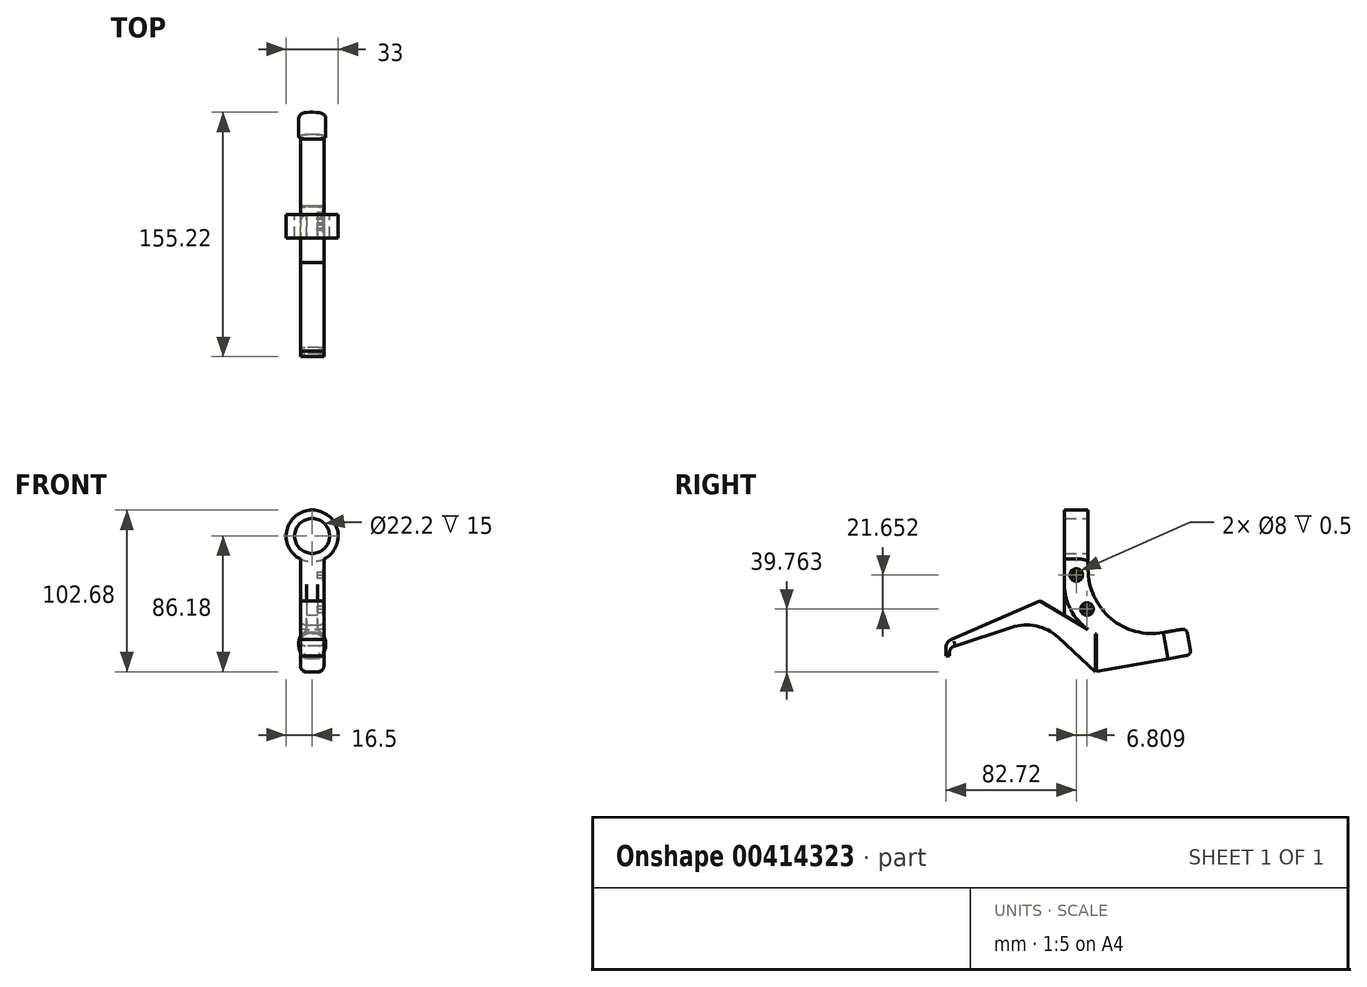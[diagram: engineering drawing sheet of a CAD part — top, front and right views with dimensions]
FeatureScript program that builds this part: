
annotation { "Feature Type Name" : "Feature", "Feature Type Description" : "" }
export const myFeature = defineFeature(function(context is Context, id is Id, definition is map)
    precondition{}
    {
        {
            var Q0;
            Q0=qCreatedBy(makeId("Front.planeOp"),FACE);
            var sketch = newSketch(context, id + "F0", { "sketchPlane" : qUnion([Q0])});
            skCircle(sketch, "E0", {"center": v(0, 0) * mm, "radius": 11.1 * mm});
            skCircle(sketch, "E1", {"center": v(0, 0) * mm, "radius": 16.5 * mm});
            skSolve(sketch);
        }
        {
            var Q0;
            Q0=makeQuery(id+"F0.imprint","IMPRINT",FACE,{"disambiguationData":[TD([[makeQuery(id+"F0.imprint","IMPRINT",EDGE,{"derivedFrom":sQuery(id+"F0.wireOp",EDGE,"E0")}),-1.0]])]});
            extrude(context, id + "F1", {"entities" : qUnion([Q0]), "endBound" : BoundingType.SYMMETRIC, "depth" : 15 * mm});
        }
        {
            var Q0;
            Q0=qCreatedBy(makeId("Right.planeOp"),FACE);
            var sketch = newSketch(context, id + "F2", { "sketchPlane" : qUnion([Q0])});
            skLineSegment(sketch, "E2", {"start": v(0, 0) * mm, "end": v(0, -54.97) * mm});
            skLineSegment(sketch, "E3", {"start": v(-7.5, 31.4) * mm, "end": v(-7.5, -50.53) * mm});
            skArc(sketch, "E4", {"start": v(-7.5, -30.7) * mm, "mid": v(-3.52, -46.9) * mm, "end": v(7.5, -59.41) * mm});
            skLineSegment(sketch, "E5", {"start": v(7.5, 51.74) * mm, "end": v(7.5, -21.27) * mm});
            skArc(sketch, "E6", {"start": v(7.5, -21.27) * mm, "mid": v(22.03, -52.44) * mm, "end": v(55.26, -61.34) * mm});
            skLineSegment(sketch, "E7", {"start": v(55.26, -61.34) * mm, "end": v(58.2, -78.08) * mm});
            skLineSegment(sketch, "E8", {"start": v(7.5, -59.41) * mm, "end": v(-23.15, -41.26) * mm});
            skLineSegment(sketch, "E9", {"start": v(-82.72, -70.49) * mm, "end": v(-82.72, -76.09) * mm});
            skLineSegment(sketch, "E10", {"start": v(-80.65, -76.09) * mm, "end": v(-80.65, -74.54) * mm});
            skLineSegment(sketch, "E11", {"start": v(-24.47, -52.49) * mm, "end": v(12.27, -86.18) * mm});
            skPoint(sketch, "E12.visualSharp", {"position": v(-80.65, -70.6) * mm});
            skArc(sketch, "E12.filletArc", {"start": v(-76.83, -69.68) * mm, "mid": v(-79.58, -71.45) * mm, "end": v(-80.65, -74.54) * mm});
            skPoint(sketch, "E13.visualSharp", {"position": v(-82.72, -66.82) * mm});
            skArc(sketch, "E13.filletArc", {"start": v(-79.22, -65.72) * mm, "mid": v(-81.75, -67.53) * mm, "end": v(-82.72, -70.49) * mm});
            skLineSegment(sketch, "E14.trimOffspring", {"start": v(12.77, -86.1) * mm, "end": v(58.2, -78.08) * mm});
            skLineSegment(sketch, "E15", {"start": v(-7.5, -13.2) * mm, "end": v(7.5, -13.2) * mm});
            skLineSegment(sketch, "E16", {"start": v(-82.72, -76.09) * mm, "end": v(-80.65, -76.09) * mm});
            skLineSegment(sketch, "E17", {"start": v(12.27, -86.18) * mm, "end": v(12.27, -62.22) * mm});
            skLineSegment(sketch, "E18", {"start": v(12.27, -62.22) * mm, "end": v(12.77, -62.22) * mm});
            skLineSegment(sketch, "E19", {"start": v(12.77, -62.22) * mm, "end": v(12.77, -86.1) * mm});
            skPoint(sketch, "E20.orphan", {"position": v(12.77, -86.18) * mm});
            skLineSegment(sketch, "E21", {"start": v(-79.22, -65.72) * mm, "end": v(-23.15, -41.26) * mm});
            skLineSegment(sketch, "E22", {"start": v(-76.83, -69.68) * mm, "end": v(-24.47, -52.49) * mm});
            skSolve(sketch);
        }
        {
            var Q0;
            {var subQ0=sQuery(id+"F2.wireOp",EDGE,"E15");var subQ1=sQuery(id+"F2.wireOp",EDGE,"E2");var subQ2=makeQuery(id+"F2.imprint","INTERSECT",VERTEX,{"derivedFrom":[subQ1,subQ0]});Q0=makeQuery(id+"F2.imprint","IMPRINT",FACE,{"disambiguationData":[TD([[makeQuery(id+"F2.imprint","IMPRINT",EDGE,{"disambiguationData":[TD([[subQ2,-1.0]])],"derivedFrom":subQ1}),-1.0]])]});}
            var Q1;
            {var subQ10=sQuery(id+"F2.wireOp",EDGE,"E6");Q1=makeQuery(id+"F2.imprint","IMPRINT",FACE,{"disambiguationData":[TD([[makeQuery(id+"F2.imprint","IMPRINT",EDGE,{"derivedFrom":subQ10}),-1.0]])]});}
            extrude(context, id + "F3", {"entities" : qUnion([Q0, Q1]), "operationType" : NewBodyOperationType.ADD, "endBound" : BoundingType.SYMMETRIC, "depth" : 15 * mm});
        }
        {
            var Q0;
            {var subQ0=sQuery(id+"F2.wireOp",EDGE,"E8");var subQ1=sQuery(id+"F2.wireOp",EDGE,"E2");var subQ2=makeQuery(id+"F2.imprint","INTERSECT",VERTEX,{"derivedFrom":[subQ1,subQ0]});Q0=makeQuery(id+"F2.imprint","IMPRINT",FACE,{"disambiguationData":[TD([[makeQuery(id+"F2.imprint","IMPRINT",EDGE,{"disambiguationData":[TD([[subQ2,1.0]])],"derivedFrom":subQ1}),-1.0]])]});}
            var Q1;
            {var subQ0=sQuery(id+"F2.wireOp",EDGE,"E8");var subQ1=sQuery(id+"F2.wireOp",EDGE,"E2");var subQ2=makeQuery(id+"F2.imprint","INTERSECT",VERTEX,{"derivedFrom":[subQ1,subQ0]});Q1=makeQuery(id+"F2.imprint","IMPRINT",FACE,{"disambiguationData":[TD([[makeQuery(id+"F2.imprint","IMPRINT",EDGE,{"disambiguationData":[TD([[subQ2,1.0]])],"derivedFrom":subQ1}),1.0]])]});}
            extrude(context, id + "F4", {"entities" : qUnion([Q0, Q1]), "operationType" : NewBodyOperationType.ADD, "endBound" : BoundingType.SYMMETRIC, "depth" : 7 * mm});
        }
        {
            var Q0;
            Q0=makeQuery(id+"F3.opExtrude","CAP_EDGE",EDGE,{"disambiguationData":[OSD([sQuery(id+"F2.wireOp",EDGE,"E6")])],"isStart":false});
            var Q1;
            Q1=makeQuery(id+"F3.opExtrude","CAP_EDGE",EDGE,{"disambiguationData":[OSD([sQuery(id+"F2.wireOp",EDGE,"E6")])],"isStart":true});
            var Q2;
            Q2=makeQuery(id+"F3.opExtrude","CAP_EDGE",EDGE,{"disambiguationData":[OSD([sQuery(id+"F2.wireOp",EDGE,"E14.trimOffspring")])],"isStart":false});
            var Q3;
            Q3=makeQuery(id+"F3.opExtrude","CAP_EDGE",EDGE,{"disambiguationData":[OSD([sQuery(id+"F2.wireOp",EDGE,"E14.trimOffspring")])],"isStart":true});
            var Q4;
            {var subQ0=sQuery(id+"F2.wireOp",EDGE,"E11");var subQ1=sQuery(id+"F2.wireOp",EDGE,"Zs4zyPn6-C5Ov-mD7S-FWXZ-QsstWJXzaYqt");Q4=makeQuery(id+"FApr9hGrNwQyOrP_1.opFillet","BLEND_EDGE",EDGE,{"blendedFrom":[makeQuery(id+"F3.opExtrude","SWEPT_EDGE",EDGE,{"disambiguationData":[OSD([subQ1,subQ0])]}),makeQuery(id+"F3.opExtrude","CAP_FACE",FACE,{"disambiguationData":[OSD([sQuery(id+"F2.wireOp",EDGE,"E3"),sQuery(id+"F2.wireOp",EDGE,"E4"),sQuery(id+"F2.wireOp",EDGE,"E5"),sQuery(id+"F2.wireOp",EDGE,"E6"),sQuery(id+"F2.wireOp",EDGE,"E7"),sQuery(id+"F2.wireOp",EDGE,"E8"),sQuery(id+"F2.wireOp",EDGE,"74US1Tta-IfNn-pP87-yXde-aIHQToQtrOJx"),sQuery(id+"F2.wireOp",EDGE,"E9"),sQuery(id+"F2.wireOp",EDGE,"E10"),subQ1,subQ0,sQuery(id+"F2.wireOp",EDGE,"E12.filletArc"),sQuery(id+"F2.wireOp",EDGE,"E13.filletArc"),sQuery(id+"F2.wireOp",EDGE,"E14.trimOffspring"),sQuery(id+"F2.wireOp",EDGE,"E15"),sQuery(id+"F2.wireOp",EDGE,"E16"),sQuery(id+"F2.wireOp",EDGE,"E17"),sQuery(id+"F2.wireOp",EDGE,"E18"),sQuery(id+"F2.wireOp",EDGE,"E19")])],"isStart":true})],"blendedInto":[makeQuery(id+"F3.opExtrude","CAP_FACE",FACE,{"disambiguationData":[OSD([sQuery(id+"F2.wireOp",EDGE,"E3"),sQuery(id+"F2.wireOp",EDGE,"E4"),sQuery(id+"F2.wireOp",EDGE,"E5"),sQuery(id+"F2.wireOp",EDGE,"E6"),sQuery(id+"F2.wireOp",EDGE,"E7"),sQuery(id+"F2.wireOp",EDGE,"E8"),sQuery(id+"F2.wireOp",EDGE,"74US1Tta-IfNn-pP87-yXde-aIHQToQtrOJx"),sQuery(id+"F2.wireOp",EDGE,"E9"),sQuery(id+"F2.wireOp",EDGE,"E10"),subQ1,subQ0,sQuery(id+"F2.wireOp",EDGE,"E12.filletArc"),sQuery(id+"F2.wireOp",EDGE,"E13.filletArc"),sQuery(id+"F2.wireOp",EDGE,"E14.trimOffspring"),sQuery(id+"F2.wireOp",EDGE,"E15"),sQuery(id+"F2.wireOp",EDGE,"E16"),sQuery(id+"F2.wireOp",EDGE,"E17"),sQuery(id+"F2.wireOp",EDGE,"E18"),sQuery(id+"F2.wireOp",EDGE,"E19")])],"isStart":true})]});}
            var Q5;
            {var subQ0=sQuery(id+"F2.wireOp",EDGE,"E11");var subQ1=sQuery(id+"F2.wireOp",EDGE,"Zs4zyPn6-C5Ov-mD7S-FWXZ-QsstWJXzaYqt");Q5=makeQuery(id+"FApr9hGrNwQyOrP_1.opFillet","BLEND_EDGE",EDGE,{"blendedFrom":[makeQuery(id+"F3.opExtrude","SWEPT_EDGE",EDGE,{"disambiguationData":[OSD([subQ1,subQ0])]}),makeQuery(id+"F3.opExtrude","CAP_FACE",FACE,{"disambiguationData":[OSD([sQuery(id+"F2.wireOp",EDGE,"E3"),sQuery(id+"F2.wireOp",EDGE,"E4"),sQuery(id+"F2.wireOp",EDGE,"E5"),sQuery(id+"F2.wireOp",EDGE,"E6"),sQuery(id+"F2.wireOp",EDGE,"E7"),sQuery(id+"F2.wireOp",EDGE,"E8"),sQuery(id+"F2.wireOp",EDGE,"74US1Tta-IfNn-pP87-yXde-aIHQToQtrOJx"),sQuery(id+"F2.wireOp",EDGE,"E9"),sQuery(id+"F2.wireOp",EDGE,"E10"),subQ1,subQ0,sQuery(id+"F2.wireOp",EDGE,"E12.filletArc"),sQuery(id+"F2.wireOp",EDGE,"E13.filletArc"),sQuery(id+"F2.wireOp",EDGE,"E14.trimOffspring"),sQuery(id+"F2.wireOp",EDGE,"E15"),sQuery(id+"F2.wireOp",EDGE,"E16"),sQuery(id+"F2.wireOp",EDGE,"E17"),sQuery(id+"F2.wireOp",EDGE,"E18"),sQuery(id+"F2.wireOp",EDGE,"E19")])],"isStart":false})],"blendedInto":[makeQuery(id+"F3.opExtrude","CAP_FACE",FACE,{"disambiguationData":[OSD([sQuery(id+"F2.wireOp",EDGE,"E3"),sQuery(id+"F2.wireOp",EDGE,"E4"),sQuery(id+"F2.wireOp",EDGE,"E5"),sQuery(id+"F2.wireOp",EDGE,"E6"),sQuery(id+"F2.wireOp",EDGE,"E7"),sQuery(id+"F2.wireOp",EDGE,"E8"),sQuery(id+"F2.wireOp",EDGE,"74US1Tta-IfNn-pP87-yXde-aIHQToQtrOJx"),sQuery(id+"F2.wireOp",EDGE,"E9"),sQuery(id+"F2.wireOp",EDGE,"E10"),subQ1,subQ0,sQuery(id+"F2.wireOp",EDGE,"E12.filletArc"),sQuery(id+"F2.wireOp",EDGE,"E13.filletArc"),sQuery(id+"F2.wireOp",EDGE,"E14.trimOffspring"),sQuery(id+"F2.wireOp",EDGE,"E15"),sQuery(id+"F2.wireOp",EDGE,"E16"),sQuery(id+"F2.wireOp",EDGE,"E17"),sQuery(id+"F2.wireOp",EDGE,"E18"),sQuery(id+"F2.wireOp",EDGE,"E19")])],"isStart":false})]});}
            fillet(context, id + "F5", {"entities" : qUnion([Q0, Q1, Q2, Q3, Q4, Q5]), "radius" : 5 * mm, "tangentPropagation" : true, "allowEdgeOverflow" : false});
        }
        {
            var Q0;
            Q0=makeQuery(id+"F3.opExtrude","SWEPT_FACE",FACE,{"disambiguationData":[OSD([sQuery(id+"F2.wireOp",EDGE,"E7")])]});
            var sketch = newSketch(context, id + "F6", { "sketchPlane" : qUnion([Q0])});
            skCircle(sketch, "E23", {"center": v(0, -78.5) * mm, "radius": 8.5 * mm});
            skPoint(sketch, "E23.centerSnap0", {"position": v(-7.5, -78.5) * mm});
            skSolve(sketch);
        }
        {
            var Q0;
            {var subQ2=sQuery(id+"F2.wireOp",EDGE,"E7");var subQ16=makeQuery(id+"F3.opExtrude","CAP_EDGE",EDGE,{"disambiguationData":[OSD([subQ2])],"isStart":true});Q0=makeQuery(id+"F6.imprint","IMPRINT",FACE,{"disambiguationData":[TD([[makeQuery(id+"F6.imprint","IMPRINT",EDGE,{"derivedFrom":subQ16}),-1.0]])]});}
            var Q1;
            {var subQ1=sQuery(id+"F2.wireOp",EDGE,"E7");var subQ7=makeQuery(id+"F3.opExtrude","CAP_EDGE",EDGE,{"disambiguationData":[OSD([subQ1])],"isStart":false});Q1=makeQuery(id+"F6.imprint","IMPRINT",FACE,{"disambiguationData":[TD([[makeQuery(id+"F6.imprint","IMPRINT",EDGE,{"derivedFrom":subQ7}),-1.0]])]});}
            var Q2;
            {var subQ1=sQuery(id+"F2.wireOp",EDGE,"E7");var subQ7=makeQuery(id+"F3.opExtrude","CAP_EDGE",EDGE,{"disambiguationData":[OSD([subQ1])],"isStart":true});Q2=makeQuery(id+"F6.imprint","IMPRINT",FACE,{"disambiguationData":[TD([[makeQuery(id+"F6.imprint","IMPRINT",EDGE,{"derivedFrom":subQ7}),1.0]])]});}
            extrude(context, id + "F7", {"entities" : qUnion([Q0, Q1, Q2]), "operationType" : NewBodyOperationType.ADD, "depth" : 15 * mm});
        }
        {
            var Q0;
            Q0=makeQuery(id+"F7.opExtrude","CAP_EDGE",EDGE,{"disambiguationData":[OSD([sQuery(id+"F6.wireOp",EDGE,"E23")])],"isStart":false});
            fillet(context, id + "F8", {"entities" : qUnion([Q0]), "radius" : 3 * mm, "tangentPropagation" : true, "allowEdgeOverflow" : false});
        }
        {
            var Q0;
            Q0=makeQuery(id+"F3.opExtrude","SWEPT_EDGE",EDGE,{"disambiguationData":[OSD([sQuery(id+"F2.wireOp",EDGE,"E11"),sQuery(id+"F2.wireOp",EDGE,"E22")])]});
            fillet(context, id + "F9", {"entities" : qUnion([Q0]), "radius" : 30 * mm, "tangentPropagation" : true, "allowEdgeOverflow" : false});
        }
        {
            var Q0;
            Q0=makeQuery(id+"F3.opExtrude","CAP_EDGE",EDGE,{"disambiguationData":[OSD([sQuery(id+"F2.wireOp",EDGE,"E11")])],"isStart":false});
            var Q1;
            Q1=makeQuery(id+"F3.opExtrude","CAP_EDGE",EDGE,{"disambiguationData":[OSD([sQuery(id+"F2.wireOp",EDGE,"E11")])],"isStart":true});
            fillet(context, id + "F10", {"entities" : qUnion([Q0, Q1]), "radius" : 3 * mm, "tangentPropagation" : true, "allowEdgeOverflow" : false});
        }
        {
            var Q0;
            Q0=makeQuery(id+"F3.opExtrude","CAP_FACE",FACE,{"disambiguationData":[OSD([sQuery(id+"F2.wireOp",EDGE,"E3"),sQuery(id+"F2.wireOp",EDGE,"E4"),sQuery(id+"F2.wireOp",EDGE,"E5"),sQuery(id+"F2.wireOp",EDGE,"E6"),sQuery(id+"F2.wireOp",EDGE,"E7"),sQuery(id+"F2.wireOp",EDGE,"E8"),sQuery(id+"F2.wireOp",EDGE,"E9"),sQuery(id+"F2.wireOp",EDGE,"E10"),sQuery(id+"F2.wireOp",EDGE,"E11"),sQuery(id+"F2.wireOp",EDGE,"E12.filletArc"),sQuery(id+"F2.wireOp",EDGE,"E13.filletArc"),sQuery(id+"F2.wireOp",EDGE,"E14.trimOffspring"),sQuery(id+"F2.wireOp",EDGE,"E15"),sQuery(id+"F2.wireOp",EDGE,"E16"),sQuery(id+"F2.wireOp",EDGE,"E17"),sQuery(id+"F2.wireOp",EDGE,"E18"),sQuery(id+"F2.wireOp",EDGE,"E19"),sQuery(id+"F2.wireOp",EDGE,"E21"),sQuery(id+"F2.wireOp",EDGE,"E22")])],"isStart":false});
            var sketch = newSketch(context, id + "F11", { "sketchPlane" : qUnion([Q0])});
            skCircle(sketch, "E24", {"center": v(0, -24.77) * mm, "radius": 4 * mm});
            skCircle(sketch, "E25", {"center": v(6.8, -46.42) * mm, "radius": 4 * mm});
            skSolve(sketch);
        }
        {
            var Q0;
            {var subQ0=sQuery(id+"F11.wireOp",EDGE,"E24");var subQ1=sQuery(id+"F2.wireOp",EDGE,"E6");var subQ2=makeQuery(id+"F5.opFillet","BLEND_EDGE",EDGE,{"blendedFrom":[makeQuery(id+"F3.opExtrude","CAP_EDGE",EDGE,{"disambiguationData":[OSD([subQ1])],"isStart":false}),makeQuery(id+"F3.opExtrude","CAP_FACE",FACE,{"disambiguationData":[OSD([sQuery(id+"F2.wireOp",EDGE,"E3"),sQuery(id+"F2.wireOp",EDGE,"E4"),sQuery(id+"F2.wireOp",EDGE,"E5"),subQ1,sQuery(id+"F2.wireOp",EDGE,"E7"),sQuery(id+"F2.wireOp",EDGE,"E8"),sQuery(id+"F2.wireOp",EDGE,"E9"),sQuery(id+"F2.wireOp",EDGE,"E10"),sQuery(id+"F2.wireOp",EDGE,"E11"),sQuery(id+"F2.wireOp",EDGE,"E12.filletArc"),sQuery(id+"F2.wireOp",EDGE,"E13.filletArc"),sQuery(id+"F2.wireOp",EDGE,"E14.trimOffspring"),sQuery(id+"F2.wireOp",EDGE,"E15"),sQuery(id+"F2.wireOp",EDGE,"E16"),sQuery(id+"F2.wireOp",EDGE,"E17"),sQuery(id+"F2.wireOp",EDGE,"E18"),sQuery(id+"F2.wireOp",EDGE,"E19"),sQuery(id+"F2.wireOp",EDGE,"E21"),sQuery(id+"F2.wireOp",EDGE,"E22")])],"isStart":false})],"blendedInto":[makeQuery(id+"F3.opExtrude","CAP_FACE",FACE,{"disambiguationData":[OSD([sQuery(id+"F2.wireOp",EDGE,"E3"),sQuery(id+"F2.wireOp",EDGE,"E4"),sQuery(id+"F2.wireOp",EDGE,"E5"),subQ1,sQuery(id+"F2.wireOp",EDGE,"E7"),sQuery(id+"F2.wireOp",EDGE,"E8"),sQuery(id+"F2.wireOp",EDGE,"E9"),sQuery(id+"F2.wireOp",EDGE,"E10"),sQuery(id+"F2.wireOp",EDGE,"E11"),sQuery(id+"F2.wireOp",EDGE,"E12.filletArc"),sQuery(id+"F2.wireOp",EDGE,"E13.filletArc"),sQuery(id+"F2.wireOp",EDGE,"E14.trimOffspring"),sQuery(id+"F2.wireOp",EDGE,"E15"),sQuery(id+"F2.wireOp",EDGE,"E16"),sQuery(id+"F2.wireOp",EDGE,"E17"),sQuery(id+"F2.wireOp",EDGE,"E18"),sQuery(id+"F2.wireOp",EDGE,"E19"),sQuery(id+"F2.wireOp",EDGE,"E21"),sQuery(id+"F2.wireOp",EDGE,"E22")])],"isStart":false})]});var subQ3=makeQuery(id+"F11.imprint","INTERSECT",VERTEX,{"disambiguationData":[OD(0.0)],"derivedFrom":[subQ2,subQ0]});Q0=makeQuery(id+"F11.imprint","IMPRINT",FACE,{"disambiguationData":[TD([[makeQuery(id+"F11.imprint","IMPRINT",EDGE,{"disambiguationData":[TD([[subQ3,1.0]])],"derivedFrom":subQ0}),1.0]])]});}
            var Q1;
            {var subQ0=sQuery(id+"F11.wireOp",EDGE,"E25");var subQ1=sQuery(id+"F2.wireOp",EDGE,"E6");var subQ2=makeQuery(id+"F5.opFillet","BLEND_EDGE",EDGE,{"blendedFrom":[makeQuery(id+"F3.opExtrude","CAP_EDGE",EDGE,{"disambiguationData":[OSD([subQ1])],"isStart":false}),makeQuery(id+"F3.opExtrude","CAP_FACE",FACE,{"disambiguationData":[OSD([sQuery(id+"F2.wireOp",EDGE,"E3"),sQuery(id+"F2.wireOp",EDGE,"E4"),sQuery(id+"F2.wireOp",EDGE,"E5"),subQ1,sQuery(id+"F2.wireOp",EDGE,"E7"),sQuery(id+"F2.wireOp",EDGE,"E8"),sQuery(id+"F2.wireOp",EDGE,"E9"),sQuery(id+"F2.wireOp",EDGE,"E10"),sQuery(id+"F2.wireOp",EDGE,"E11"),sQuery(id+"F2.wireOp",EDGE,"E12.filletArc"),sQuery(id+"F2.wireOp",EDGE,"E13.filletArc"),sQuery(id+"F2.wireOp",EDGE,"E14.trimOffspring"),sQuery(id+"F2.wireOp",EDGE,"E15"),sQuery(id+"F2.wireOp",EDGE,"E16"),sQuery(id+"F2.wireOp",EDGE,"E17"),sQuery(id+"F2.wireOp",EDGE,"E18"),sQuery(id+"F2.wireOp",EDGE,"E19"),sQuery(id+"F2.wireOp",EDGE,"E21"),sQuery(id+"F2.wireOp",EDGE,"E22")])],"isStart":false})],"blendedInto":[makeQuery(id+"F3.opExtrude","CAP_FACE",FACE,{"disambiguationData":[OSD([sQuery(id+"F2.wireOp",EDGE,"E3"),sQuery(id+"F2.wireOp",EDGE,"E4"),sQuery(id+"F2.wireOp",EDGE,"E5"),subQ1,sQuery(id+"F2.wireOp",EDGE,"E7"),sQuery(id+"F2.wireOp",EDGE,"E8"),sQuery(id+"F2.wireOp",EDGE,"E9"),sQuery(id+"F2.wireOp",EDGE,"E10"),sQuery(id+"F2.wireOp",EDGE,"E11"),sQuery(id+"F2.wireOp",EDGE,"E12.filletArc"),sQuery(id+"F2.wireOp",EDGE,"E13.filletArc"),sQuery(id+"F2.wireOp",EDGE,"E14.trimOffspring"),sQuery(id+"F2.wireOp",EDGE,"E15"),sQuery(id+"F2.wireOp",EDGE,"E16"),sQuery(id+"F2.wireOp",EDGE,"E17"),sQuery(id+"F2.wireOp",EDGE,"E18"),sQuery(id+"F2.wireOp",EDGE,"E19"),sQuery(id+"F2.wireOp",EDGE,"E21"),sQuery(id+"F2.wireOp",EDGE,"E22")])],"isStart":false})]});var subQ3=makeQuery(id+"F11.imprint","INTERSECT",VERTEX,{"disambiguationData":[OD(0.0)],"derivedFrom":[subQ2,subQ0]});Q1=makeQuery(id+"F11.imprint","IMPRINT",FACE,{"disambiguationData":[TD([[makeQuery(id+"F11.imprint","IMPRINT",EDGE,{"disambiguationData":[TD([[subQ3,-1.0]])],"derivedFrom":subQ0}),1.0]])]});}
            var Q2;
            {var subQ0=sQuery(id+"F11.wireOp",EDGE,"E25");var subQ1=sQuery(id+"F2.wireOp",EDGE,"E6");var subQ2=makeQuery(id+"F5.opFillet","BLEND_EDGE",EDGE,{"blendedFrom":[makeQuery(id+"F3.opExtrude","CAP_EDGE",EDGE,{"disambiguationData":[OSD([subQ1])],"isStart":false}),makeQuery(id+"F3.opExtrude","CAP_FACE",FACE,{"disambiguationData":[OSD([sQuery(id+"F2.wireOp",EDGE,"E3"),sQuery(id+"F2.wireOp",EDGE,"E4"),sQuery(id+"F2.wireOp",EDGE,"E5"),subQ1,sQuery(id+"F2.wireOp",EDGE,"E7"),sQuery(id+"F2.wireOp",EDGE,"E8"),sQuery(id+"F2.wireOp",EDGE,"E9"),sQuery(id+"F2.wireOp",EDGE,"E10"),sQuery(id+"F2.wireOp",EDGE,"E11"),sQuery(id+"F2.wireOp",EDGE,"E12.filletArc"),sQuery(id+"F2.wireOp",EDGE,"E13.filletArc"),sQuery(id+"F2.wireOp",EDGE,"E14.trimOffspring"),sQuery(id+"F2.wireOp",EDGE,"E15"),sQuery(id+"F2.wireOp",EDGE,"E16"),sQuery(id+"F2.wireOp",EDGE,"E17"),sQuery(id+"F2.wireOp",EDGE,"E18"),sQuery(id+"F2.wireOp",EDGE,"E19"),sQuery(id+"F2.wireOp",EDGE,"E21"),sQuery(id+"F2.wireOp",EDGE,"E22")])],"isStart":false})],"blendedInto":[makeQuery(id+"F3.opExtrude","CAP_FACE",FACE,{"disambiguationData":[OSD([sQuery(id+"F2.wireOp",EDGE,"E3"),sQuery(id+"F2.wireOp",EDGE,"E4"),sQuery(id+"F2.wireOp",EDGE,"E5"),subQ1,sQuery(id+"F2.wireOp",EDGE,"E7"),sQuery(id+"F2.wireOp",EDGE,"E8"),sQuery(id+"F2.wireOp",EDGE,"E9"),sQuery(id+"F2.wireOp",EDGE,"E10"),sQuery(id+"F2.wireOp",EDGE,"E11"),sQuery(id+"F2.wireOp",EDGE,"E12.filletArc"),sQuery(id+"F2.wireOp",EDGE,"E13.filletArc"),sQuery(id+"F2.wireOp",EDGE,"E14.trimOffspring"),sQuery(id+"F2.wireOp",EDGE,"E15"),sQuery(id+"F2.wireOp",EDGE,"E16"),sQuery(id+"F2.wireOp",EDGE,"E17"),sQuery(id+"F2.wireOp",EDGE,"E18"),sQuery(id+"F2.wireOp",EDGE,"E19"),sQuery(id+"F2.wireOp",EDGE,"E21"),sQuery(id+"F2.wireOp",EDGE,"E22")])],"isStart":false})]});var subQ3=makeQuery(id+"F11.imprint","INTERSECT",VERTEX,{"disambiguationData":[OD(0.0)],"derivedFrom":[subQ2,subQ0]});Q2=makeQuery(id+"F11.imprint","IMPRINT",FACE,{"disambiguationData":[TD([[makeQuery(id+"F11.imprint","IMPRINT",EDGE,{"disambiguationData":[TD([[subQ3,1.0]])],"derivedFrom":subQ0}),1.0]])]});}
            var Q3;
            {var subQ0=sQuery(id+"F11.wireOp",EDGE,"E24");var subQ1=sQuery(id+"F2.wireOp",EDGE,"E6");var subQ2=makeQuery(id+"F5.opFillet","BLEND_EDGE",EDGE,{"blendedFrom":[makeQuery(id+"F3.opExtrude","CAP_EDGE",EDGE,{"disambiguationData":[OSD([subQ1])],"isStart":false}),makeQuery(id+"F3.opExtrude","CAP_FACE",FACE,{"disambiguationData":[OSD([sQuery(id+"F2.wireOp",EDGE,"E3"),sQuery(id+"F2.wireOp",EDGE,"E4"),sQuery(id+"F2.wireOp",EDGE,"E5"),subQ1,sQuery(id+"F2.wireOp",EDGE,"E7"),sQuery(id+"F2.wireOp",EDGE,"E8"),sQuery(id+"F2.wireOp",EDGE,"E9"),sQuery(id+"F2.wireOp",EDGE,"E10"),sQuery(id+"F2.wireOp",EDGE,"E11"),sQuery(id+"F2.wireOp",EDGE,"E12.filletArc"),sQuery(id+"F2.wireOp",EDGE,"E13.filletArc"),sQuery(id+"F2.wireOp",EDGE,"E14.trimOffspring"),sQuery(id+"F2.wireOp",EDGE,"E15"),sQuery(id+"F2.wireOp",EDGE,"E16"),sQuery(id+"F2.wireOp",EDGE,"E17"),sQuery(id+"F2.wireOp",EDGE,"E18"),sQuery(id+"F2.wireOp",EDGE,"E19"),sQuery(id+"F2.wireOp",EDGE,"E21"),sQuery(id+"F2.wireOp",EDGE,"E22")])],"isStart":false})],"blendedInto":[makeQuery(id+"F3.opExtrude","CAP_FACE",FACE,{"disambiguationData":[OSD([sQuery(id+"F2.wireOp",EDGE,"E3"),sQuery(id+"F2.wireOp",EDGE,"E4"),sQuery(id+"F2.wireOp",EDGE,"E5"),subQ1,sQuery(id+"F2.wireOp",EDGE,"E7"),sQuery(id+"F2.wireOp",EDGE,"E8"),sQuery(id+"F2.wireOp",EDGE,"E9"),sQuery(id+"F2.wireOp",EDGE,"E10"),sQuery(id+"F2.wireOp",EDGE,"E11"),sQuery(id+"F2.wireOp",EDGE,"E12.filletArc"),sQuery(id+"F2.wireOp",EDGE,"E13.filletArc"),sQuery(id+"F2.wireOp",EDGE,"E14.trimOffspring"),sQuery(id+"F2.wireOp",EDGE,"E15"),sQuery(id+"F2.wireOp",EDGE,"E16"),sQuery(id+"F2.wireOp",EDGE,"E17"),sQuery(id+"F2.wireOp",EDGE,"E18"),sQuery(id+"F2.wireOp",EDGE,"E19"),sQuery(id+"F2.wireOp",EDGE,"E21"),sQuery(id+"F2.wireOp",EDGE,"E22")])],"isStart":false})]});var subQ3=makeQuery(id+"F11.imprint","INTERSECT",VERTEX,{"disambiguationData":[OD(0.0)],"derivedFrom":[subQ2,subQ0]});Q3=makeQuery(id+"F11.imprint","IMPRINT",FACE,{"disambiguationData":[TD([[makeQuery(id+"F11.imprint","IMPRINT",EDGE,{"disambiguationData":[TD([[subQ3,-1.0]])],"derivedFrom":subQ0}),1.0]])]});}
            extrude(context, id + "F12", {"entities" : qUnion([Q0, Q1, Q2, Q3]), "operationType" : NewBodyOperationType.REMOVE, "oppositeDirection" : true, "depth" : 0.5 * mm});
        }
        {
            var Q0;
            Q0=makeQuery(id+"F12.boolean.opBoolean","COPY",FACE,{"derivedFrom":makeQuery(id+"F12.opExtrude","CAP_FACE",FACE,{"disambiguationData":[OSD([sQuery(id+"F11.wireOp",EDGE,"E24")])],"isStart":false})});
            var sketch = newSketch(context, id + "F13", { "sketchPlane" : qUnion([Q0])});
            skCircle(sketch, "E26.cCircle", {"center": v(0, -24.77) * mm, "radius": 2 * mm, "construction": true});
            skLineSegment(sketch, "E26.0", {"start": v(1.15, -26.77) * mm, "end": v(-1.15, -26.77) * mm});
            skLineSegment(sketch, "E26.1", {"start": v(-1.15, -26.77) * mm, "end": v(-2.3, -24.77) * mm});
            skLineSegment(sketch, "E26.2", {"start": v(-2.3, -24.77) * mm, "end": v(-1.15, -22.77) * mm});
            skLineSegment(sketch, "E26.3", {"start": v(-1.15, -22.77) * mm, "end": v(1.15, -22.77) * mm});
            skLineSegment(sketch, "E26.4", {"start": v(1.15, -22.77) * mm, "end": v(2.3, -24.77) * mm});
            skLineSegment(sketch, "E26.5", {"start": v(2.3, -24.77) * mm, "end": v(1.15, -26.77) * mm});
            skPoint(sketch, "E26.0.midPoint", {"position": v(0, -26.77) * mm});
            skSolve(sketch);
        }
        {
            var Q0;
            Q0=makeQuery(id+"F13.imprint","IMPRINT",FACE,{"disambiguationData":[TD([[makeQuery(id+"F13.imprint","IMPRINT",EDGE,{"derivedFrom":sQuery(id+"F13.wireOp",EDGE,"E26.0")}),-1.0]])]});
            extrude(context, id + "F14", {"entities" : qUnion([Q0]), "operationType" : NewBodyOperationType.REMOVE, "oppositeDirection" : true, "depth" : 4 * mm});
        }
        {
            var Q0;
            Q0=makeQuery(id+"F12.boolean.opBoolean","COPY",FACE,{"derivedFrom":makeQuery(id+"F12.opExtrude","CAP_FACE",FACE,{"disambiguationData":[OSD([sQuery(id+"F11.wireOp",EDGE,"E25")])],"isStart":false})});
            var sketch = newSketch(context, id + "F15", { "sketchPlane" : qUnion([Q0])});
            skCircle(sketch, "E27.cCircle", {"center": v(6.8, -46.42) * mm, "radius": 2 * mm, "construction": true});
            skLineSegment(sketch, "E27.0", {"start": v(7.96, -48.42) * mm, "end": v(5.65, -48.42) * mm});
            skLineSegment(sketch, "E27.1", {"start": v(5.65, -48.42) * mm, "end": v(4.5, -46.42) * mm});
            skLineSegment(sketch, "E27.2", {"start": v(4.5, -46.42) * mm, "end": v(5.65, -44.42) * mm});
            skLineSegment(sketch, "E27.3", {"start": v(5.65, -44.42) * mm, "end": v(7.96, -44.42) * mm});
            skLineSegment(sketch, "E27.4", {"start": v(7.96, -44.42) * mm, "end": v(9.12, -46.42) * mm});
            skLineSegment(sketch, "E27.5", {"start": v(9.12, -46.42) * mm, "end": v(7.96, -48.42) * mm});
            skPoint(sketch, "E27.0.midPoint", {"position": v(6.8, -48.42) * mm});
            skSolve(sketch);
        }
        {
            var Q0;
            Q0=makeQuery(id+"F15.imprint","IMPRINT",FACE,{"disambiguationData":[TD([[makeQuery(id+"F15.imprint","IMPRINT",EDGE,{"derivedFrom":sQuery(id+"F15.wireOp",EDGE,"E27.0")}),-1.0]])]});
            extrude(context, id + "F16", {"entities" : qUnion([Q0]), "operationType" : NewBodyOperationType.REMOVE, "oppositeDirection" : true, "depth" : 4 * mm});
        }
    });
